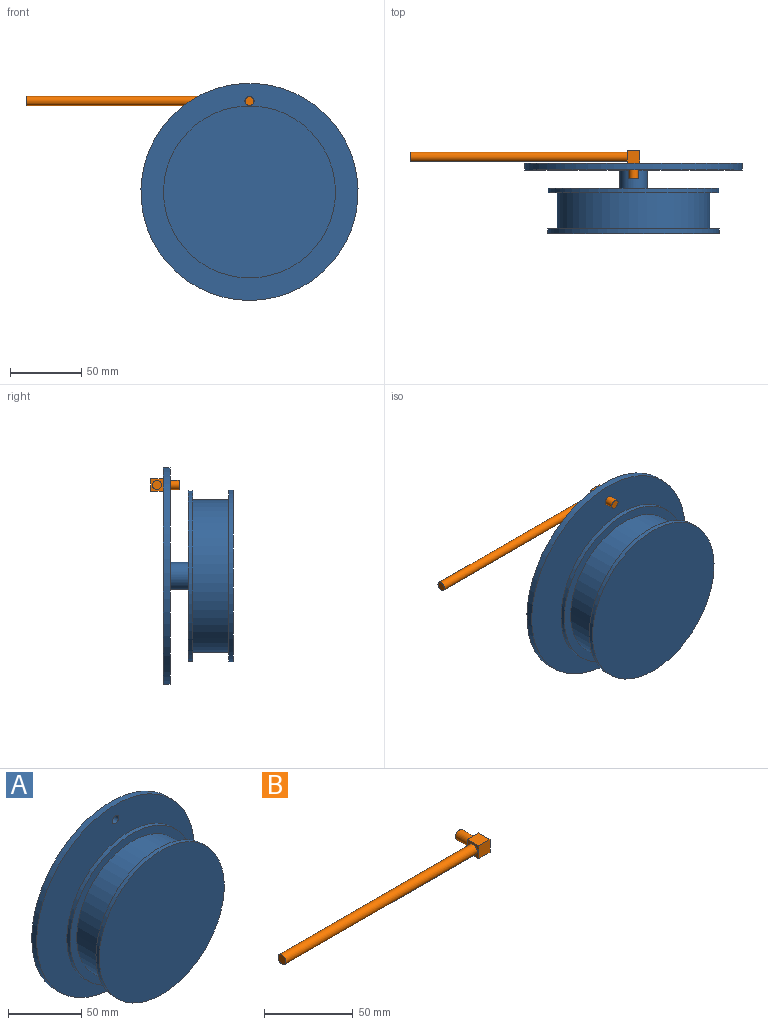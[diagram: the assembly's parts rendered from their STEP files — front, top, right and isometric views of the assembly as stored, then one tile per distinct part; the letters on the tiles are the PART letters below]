
ASSEMBLY  parts=2 mates=1
PART A: 15 faces, bbox 152.4x49.2x152.4 mm
  f0: cylinder r=3.17mm len=6.35mm, axis (0,1,0), area 95mm2, adj f2,f3
  f1: cylinder r=76.2mm len=152.4mm, axis (0,1,0), area 2280.2mm2, adj f2,f3
  f2: plane 152.4x152.4mm, normal (0,-1,0), area 17924.8mm2, adj f0,f1,f4
  f3: plane 152.4x152.4mm, normal (0,1,0), area 18209.8mm2, adj f0,f1
  f4: cylinder r=9.53mm len=19.05mm, axis (0,1,0), area 760.1mm2, adj f2,f7
  f5: cylinder r=59.85mm len=119.7mm, axis (0,1,0), area 1194mm2, adj f6,f7
  f6: plane 119.7x119.7mm, normal (0,-1,0), area 2261.2mm2, adj f5,f8
  f7: plane 119.7x119.7mm, normal (0,1,0), area 10968.3mm2, adj f4,f5
  f8: cylinder r=53.5mm len=107mm, axis (0,1,0), area 8538.2mm2, adj f6,f9
  f9: plane 120.65x120.65mm, normal (0,1,0), area 2440.5mm2, adj f8,f11
  f10: plane 120.65x120.65mm, normal (0,-1,0), area 11432.6mm2, adj f11
  f11: cylinder r=60.32mm len=120.65mm, axis (0,1,0), area 1203.4mm2, adj f9,f10
  f12: plane 100.65x100.65mm, normal (0,-1,0), area 7956.4mm2, adj f13
  f13: cylinder r=50.33mm len=100.65mm, axis (0,1,0), area 8031.5mm2, adj f12,f14
  f14: plane 100.65x100.65mm, normal (0,1,0), area 7956.4mm2, adj f13
PART B: 10 faces, bbox 161.3x20x8.9 mm
  f0: cylinder r=3.17mm len=11.11mm, axis (0,1,0), area 221.7mm2, adj f1,f7
  f1: plane 6.35x6.35mm, normal (0,1,0), area 31.7mm2, adj f0
  f2: plane 8.89x8.89mm, normal (0,0,-1), area 79mm2, adj f3,f5,f6,f7
  f3: plane 8.89x8.89mm, normal (1,0,0), area 79mm2, adj f2,f4,f6,f7
  f4: plane 8.89x8.89mm, normal (0,0,1), area 79mm2, adj f3,f5,f6,f7
  f5: plane 8.89x8.89mm, normal (-1,0,0), area 47.4mm2, adj f2,f4,f6,f7,f8
  f6: plane 8.89x8.89mm, normal (0,-1,0), area 79mm2, adj f2,f3,f4,f5
  f7: plane 8.89x8.89mm, normal (0,1,0), area 47.4mm2, adj f0,f2,f3,f4,f5
  f8: cylinder r=3.17mm len=152.4mm, axis (1,0,0), area 3040.2mm2, adj f5,f9
  f9: plane 6.35x6.35mm, normal (-1,0,0), area 31.7mm2, adj f8
PLACE A t=(-39.77,-4.75,-9.59)mm
PLACE B rot(axis=(1,0,0),180deg) t=(-39.77,-15.86,54.2)mm
MATE revolute B.f0 <-> A.f0  axis (0,-1,0) through (-39.77,-4.75,54.2)mm
